# Revit family: 3468A_NX_Contact_Closure_Interface
name_source: partatom
category: Communication Devices
units: mm (PartAtom-declared; Revit-internal decimal feet)

## family parameters
Cut with Voids When Loaded = No
Host = Face
Maintain Annotation Orientation = No
OmniClass Number = 23.85.80.11.27
OmniClass Title = Lighting Controls
Part Type = Normal
Room Calculation Point = No
Round Connector Dimension = Use Diameter
Shared = Yes

## types (1)
- 3468A_NX_Contact_Closure_Interface
    Apparent Load = 0 VA
    Assembly Code = D5090
    Black Material = Paint -  Black Matte Textured
    Default Elevation = 48 "
    Description = NX Contact Closure Interface allows third party devices to
provide dry contact inputs to an NX distributed control system.
    Features = • Mounts to standard 4 11/16” junction box, Raco #257 or similar
(not supplied)
• Removable terminal block for input connection
• Connects to and is powered by NXSP SmartPORT™
• Functions include: On/Off (standard), toggle On/Off, preset, raise,
lower, timed On
• Pilot light output terminals
• Low voltage device: 24 VDC
    Green Element = Plastic - Green
    Manufacturer = NX Lighting Controls
    Model = NX Contact closure Interface
    Steel = Metal-Galvanized_Steel
    Type Comments = NX Contact closure Interface
    URL = https://www.currentlighting.com
    Voltage = 24 V
    Warranty = 5-Years Warranty
    White Element = Glass, White, High Luminance

## geometry (parser evidence)
native form markers: Sweep x3
no freeform markers — native parametric forms only
